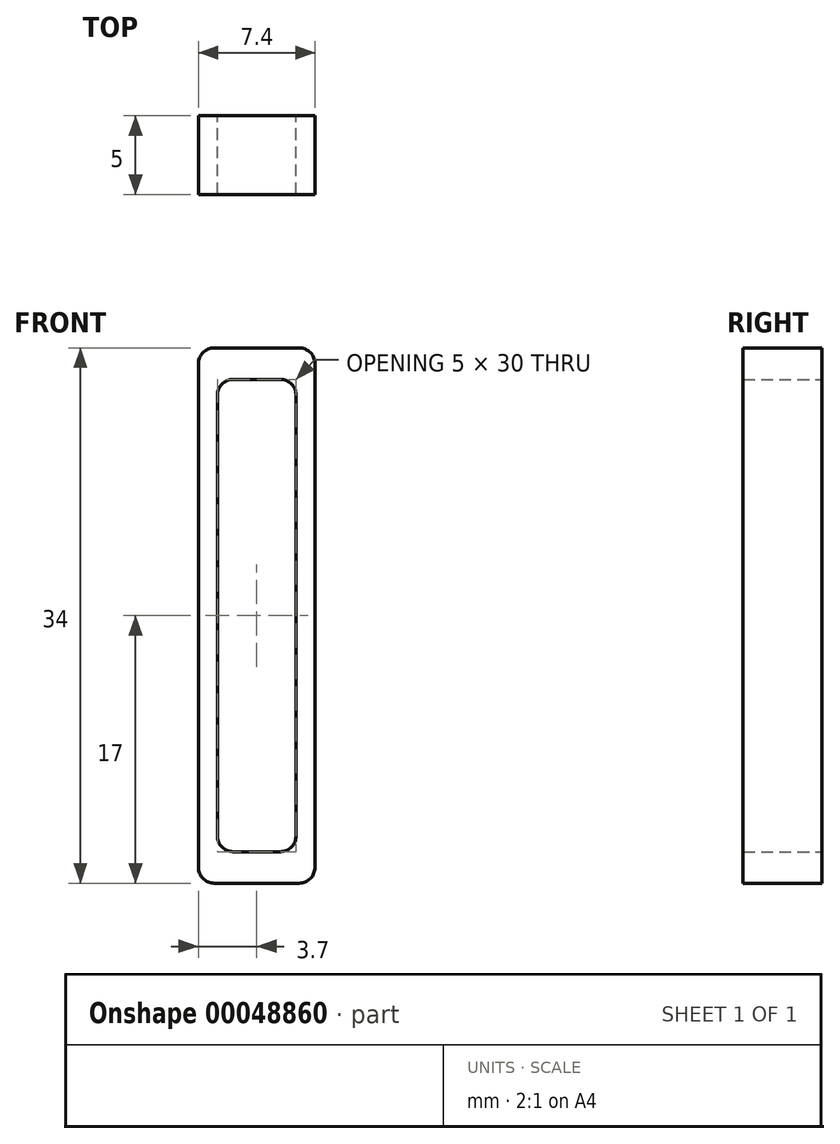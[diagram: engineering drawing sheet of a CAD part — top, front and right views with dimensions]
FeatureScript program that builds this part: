
annotation { "Feature Type Name" : "Feature", "Feature Type Description" : "" }
export const myFeature = defineFeature(function(context is Context, id is Id, definition is map)
    precondition{}
    {
        {
            var Q0;
            Q0=qCreatedBy(makeId("Front.planeOp"),FACE);
            var sketch = newSketch(context, id + "F0", { "sketchPlane" : qUnion([Q0])});
            skLineSegment(sketch, "E0.rect.bottom", {"start": v(2.5, -15) * mm, "end": v(-2.5, -15) * mm});
            skLineSegment(sketch, "E0.rect.top", {"start": v(2.5, 15) * mm, "end": v(-2.5, 15) * mm});
            skLineSegment(sketch, "E0.rect.left", {"start": v(2.5, -15) * mm, "end": v(2.5, 15) * mm});
            skLineSegment(sketch, "E0.rect.right", {"start": v(-2.5, -15) * mm, "end": v(-2.5, 15) * mm});
            skPoint(sketch, "E0.rect.middle", {"position": v(0, 0) * mm});
            skLineSegment(sketch, "E1.rect.bottom", {"start": v(-3.7, -17) * mm, "end": v(3.7, -17) * mm});
            skLineSegment(sketch, "E1.rect.top", {"start": v(-3.7, 17) * mm, "end": v(3.7, 17) * mm});
            skLineSegment(sketch, "E1.rect.left", {"start": v(-3.7, -17) * mm, "end": v(-3.7, 17) * mm});
            skLineSegment(sketch, "E1.rect.right", {"start": v(3.7, -17) * mm, "end": v(3.7, 17) * mm});
            skSolve(sketch);
        }
        {
            var Q0;
            Q0=makeQuery(id+"F0.imprint","IMPRINT",FACE,{"disambiguationData":[TD([[makeQuery(id+"F0.imprint","IMPRINT",EDGE,{"derivedFrom":sQuery(id+"F0.wireOp",EDGE,"E0.rect.bottom")}),1.0]])]});
            extrude(context, id + "F1", {"entities" : qUnion([Q0]), "depth" : 5 * mm});
        }
        {
            var Q0;
            Q0=makeQuery(id+"F1.opExtrude","SWEPT_EDGE",EDGE,{"disambiguationData":[OSD([sQuery(id+"F0.wireOp",EDGE,"E1.rect.top"),sQuery(id+"F0.wireOp",EDGE,"E1.rect.right")])]});
            var Q1;
            Q1=makeQuery(id+"F1.opExtrude","SWEPT_EDGE",EDGE,{"disambiguationData":[OSD([sQuery(id+"F0.wireOp",EDGE,"E1.rect.top"),sQuery(id+"F0.wireOp",EDGE,"E1.rect.left")])]});
            var Q2;
            Q2=makeQuery(id+"F1.opExtrude","SWEPT_EDGE",EDGE,{"disambiguationData":[OSD([sQuery(id+"F0.wireOp",EDGE,"E1.rect.bottom"),sQuery(id+"F0.wireOp",EDGE,"E1.rect.left")])]});
            var Q3;
            Q3=makeQuery(id+"F1.opExtrude","SWEPT_EDGE",EDGE,{"disambiguationData":[OSD([sQuery(id+"F0.wireOp",EDGE,"E1.rect.bottom"),sQuery(id+"F0.wireOp",EDGE,"E1.rect.right")])]});
            var Q4;
            Q4=makeQuery(id+"F1.opExtrude","SWEPT_EDGE",EDGE,{"disambiguationData":[OSD([sQuery(id+"F0.wireOp",EDGE,"E0.rect.top"),sQuery(id+"F0.wireOp",EDGE,"E0.rect.right")])]});
            var Q5;
            Q5=makeQuery(id+"F1.opExtrude","SWEPT_EDGE",EDGE,{"disambiguationData":[OSD([sQuery(id+"F0.wireOp",EDGE,"E0.rect.top"),sQuery(id+"F0.wireOp",EDGE,"E0.rect.left")])]});
            var Q6;
            Q6=makeQuery(id+"F1.opExtrude","SWEPT_EDGE",EDGE,{"disambiguationData":[OSD([sQuery(id+"F0.wireOp",EDGE,"E0.rect.bottom"),sQuery(id+"F0.wireOp",EDGE,"E0.rect.right")])]});
            var Q7;
            Q7=makeQuery(id+"F1.opExtrude","SWEPT_EDGE",EDGE,{"disambiguationData":[OSD([sQuery(id+"F0.wireOp",EDGE,"E0.rect.bottom"),sQuery(id+"F0.wireOp",EDGE,"E0.rect.left")])]});
            fillet(context, id + "F2", {"entities" : qUnion([Q0, Q1, Q2, Q3, Q4, Q5, Q6, Q7]), "radius" : 1 * mm, "tangentPropagation" : true, "allowEdgeOverflow" : false});
        }
    });
